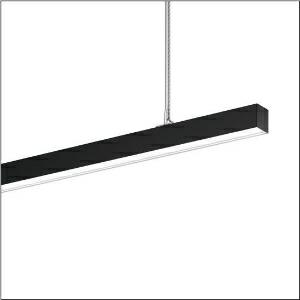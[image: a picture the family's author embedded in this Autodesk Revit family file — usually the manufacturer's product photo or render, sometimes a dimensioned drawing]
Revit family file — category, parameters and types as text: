
# Revit family: silica_21_51mx33tbt9b
name_source: partatom
category: Lighting Fixtures
units: mm (PartAtom-declared; Revit-internal decimal feet)

## family parameters
Cut with Voids When Loaded = No
Host = Face
Light Source = No
Part Type = Normal
Room Calculation Point = No
Round Connector Dimension = Use Diameter
Shared = No

## types (1)
- --- (1 x LED, 7170 lm, 67.4 W, 6500K)
    Apparent Load = 67 VA
    CIE Flux Codes = 78 96 99 56 100
    Color Rendering = 80
    Color Temperature = 6500K
    Default Elevation = 1800 mm
    Description = Silica 21, office luminaire, primary optical cover: prismatic diffuser, of PMMA, CAT 2 (L<= 3000cd/m²), light emission: direct/indirect distribution, primary light characteristic: symmetric, installation type: suspended mounting, LED, rated luminous flux: 7.170lm, luminous efficacy: 101lm/W, light colour: 8tw, colour temperature: 2700..6500K, control gear: DALI DT8, with terminal, 3+2-pole, max. 2.5mm², mains connection: 220..240V, AC, 50/60Hz, rated input power: 70.8W, luminaire housing, of aluminium, matt jet black (RAL 9005), length: 1.504mm, width: 53mm, height: 53mm, protection rating (complete): IP20, insulation class (complete): insulation class I (protective earthing), certification: CE, permissible operating ambient temperature: 0..+35°C, standard: EN 50419, packaging unit: 1 piece
    Height = 53 mm
    Lamp = 1 x LED
    Lamp Light Flux = 7170 lm
    Lamp Power = 67.4 W
    Lamp count = 1
    Length = 1504 mm
    Luminous efficacy = 106 lm/W
    Manufacturer = Siteco
    ModVariant = No
    Model = 51MX33TBT9B
    Mounting Place = Ceiling
    Mounting Type = Pendant
    Number of Poles = 1
    OnlyDefault = Yes
    Power Factor = 1
    Product Name = Silica 21
    Product group = office luminaire | ceiling pendant
    ProductGroupID = 903
    Protection Class = Protection class I
    Protection Degree = IP 20
    RLX_Detail_Level = 1
    RLX_Emergency_Light_Flux = 0 lm
    RLX_Emergency_Type = 0
    RLX_Emergency_Type_DB = No
    RlxData = <blob elided: 22909 chars, md5=bc5be9f7>
    Socket = socket
    Standby Power = 0 W
    System Light Flux = 7170 lm
    System Power = 67 W
    Type Comments = individual setting
    Type Image = l_1335856.jpg
    URL = http://relux.com
    VarID = @adj_139253
    Voltage = 0 V
    Weight = 0.00 kg
    Width = 53 mm

## geometry (parser evidence)
native form markers: Blend x4, Sweep x14
no freeform markers — native parametric forms only
